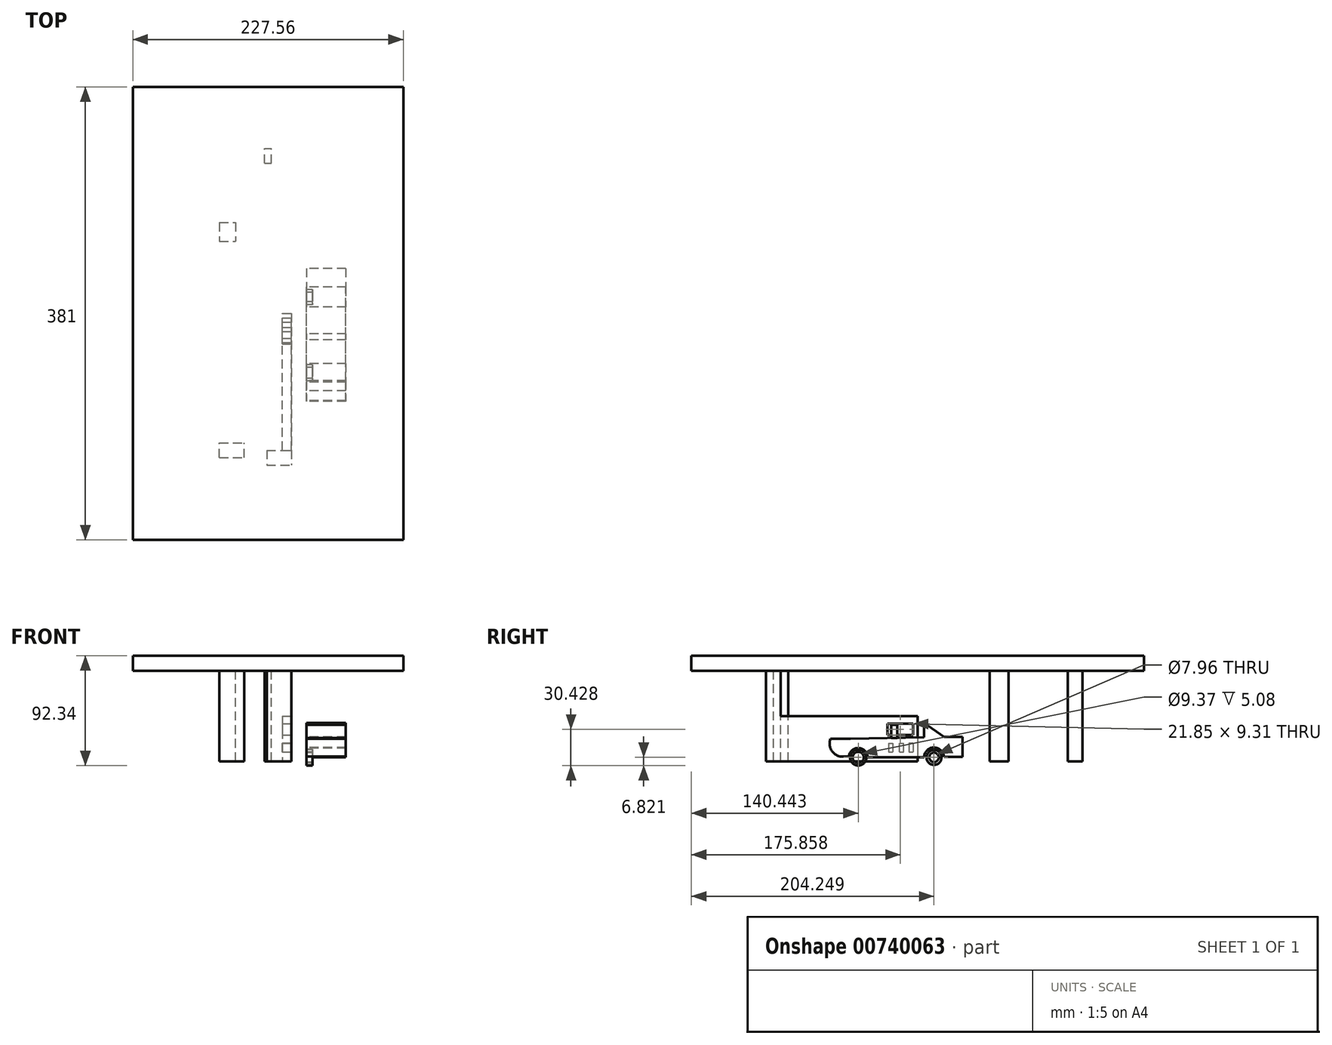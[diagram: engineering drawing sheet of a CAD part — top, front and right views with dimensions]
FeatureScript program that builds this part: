
annotation { "Feature Type Name" : "Feature", "Feature Type Description" : "" }
export const myFeature = defineFeature(function(context is Context, id is Id, definition is map)
    precondition{}
    {
        {
            var Q0;
            Q0=qCreatedBy(makeId("Top.planeOp"),FACE);
            var sketch = newSketch(context, id + "F0", { "sketchPlane" : qUnion([Q0])});
            skLineSegment(sketch, "E0.bottom", {"start": v(113.78, 190.5) * mm, "end": v(-113.78, 190.5) * mm});
            skLineSegment(sketch, "E0.top", {"start": v(113.78, -190.5) * mm, "end": v(-113.78, -190.5) * mm});
            skLineSegment(sketch, "E0.left", {"start": v(113.78, 190.5) * mm, "end": v(113.78, -190.5) * mm});
            skLineSegment(sketch, "E0.right", {"start": v(-113.78, 190.5) * mm, "end": v(-113.78, -190.5) * mm});
            skPoint(sketch, "E0.middle", {"position": v(0, 0) * mm});
            skSolve(sketch);
        }
        {
            var Q0;
            Q0=makeQuery(id+"F0.imprint","IMPRINT",FACE,{"disambiguationData":[TD([[makeQuery(id+"F0.imprint","IMPRINT",EDGE,{"derivedFrom":sQuery(id+"F0.wireOp",EDGE,"E0.bottom")}),1.0]])]});
            extrude(context, id + "F1", {"entities" : qUnion([Q0]), "depth" : 12.7 * mm, "offsetDistance" : 25.4 * mm});
        }
        {
            var Q0;
            Q0=makeQuery(id+"F1.opExtrude","CAP_FACE",FACE,{"disambiguationData":[OSD([sQuery(id+"F0.wireOp",EDGE,"E0.bottom"),sQuery(id+"F0.wireOp",EDGE,"E0.top"),sQuery(id+"F0.wireOp",EDGE,"E0.left"),sQuery(id+"F0.wireOp",EDGE,"E0.right")])],"isStart":true});
            var sketch = newSketch(context, id + "F2", { "sketchPlane" : qUnion([Q0])});
            skLineSegment(sketch, "E1.bottom", {"start": v(-2.86, -126.27) * mm, "end": v(2.86, -126.27) * mm});
            skLineSegment(sketch, "E1.top", {"start": v(-2.86, -138.66) * mm, "end": v(2.86, -138.66) * mm});
            skLineSegment(sketch, "E1.left", {"start": v(-2.86, -126.27) * mm, "end": v(-2.86, -138.66) * mm});
            skLineSegment(sketch, "E1.right", {"start": v(2.86, -126.27) * mm, "end": v(2.86, -138.66) * mm});
            skPoint(sketch, "E1.middle", {"position": v(0, -132.46) * mm});
            skLineSegment(sketch, "E2.bottom", {"start": v(-41.04, -76.38) * mm, "end": v(-27.55, -76.38) * mm});
            skLineSegment(sketch, "E2.top", {"start": v(-41.04, -60.63) * mm, "end": v(-27.55, -60.63) * mm});
            skLineSegment(sketch, "E2.left", {"start": v(-41.04, -76.38) * mm, "end": v(-41.04, -60.63) * mm});
            skLineSegment(sketch, "E2.right", {"start": v(-27.55, -76.38) * mm, "end": v(-27.55, -60.63) * mm});
            skPoint(sketch, "E2.middle", {"position": v(-34.3, -68.5) * mm});
            skLineSegment(sketch, "E3.bottom", {"start": v(-1.12, 115.21) * mm, "end": v(19.65, 115.21) * mm});
            skLineSegment(sketch, "E3.top", {"start": v(-1.12, 127.6) * mm, "end": v(19.65, 127.6) * mm});
            skLineSegment(sketch, "E3.left", {"start": v(-1.12, 115.21) * mm, "end": v(-1.12, 127.6) * mm});
            skLineSegment(sketch, "E3.right", {"start": v(19.65, 115.21) * mm, "end": v(19.65, 127.6) * mm});
            skPoint(sketch, "E3.middle", {"position": v(9.26, 121.4) * mm});
            skLineSegment(sketch, "E4.bottom", {"start": v(-41.04, 121.4) * mm, "end": v(-20.26, 121.4) * mm});
            skLineSegment(sketch, "E4.top", {"start": v(-41.04, 109.02) * mm, "end": v(-20.26, 109.02) * mm});
            skLineSegment(sketch, "E4.left", {"start": v(-41.04, 121.4) * mm, "end": v(-41.04, 109.02) * mm});
            skLineSegment(sketch, "E4.right", {"start": v(-20.26, 121.4) * mm, "end": v(-20.26, 109.02) * mm});
            skPoint(sketch, "E4.middle", {"position": v(-30.65, 115.21) * mm});
            skSolve(sketch);
        }
        {
            var Q0;
            Q0=makeQuery(id+"F2.imprint","IMPRINT",FACE,{"disambiguationData":[TD([[makeQuery(id+"F2.imprint","IMPRINT",EDGE,{"derivedFrom":sQuery(id+"F2.wireOp",EDGE,"E1.bottom")}),-1.0]])]});
            var Q1;
            Q1=makeQuery(id+"F2.imprint","IMPRINT",FACE,{"disambiguationData":[TD([[makeQuery(id+"F2.imprint","IMPRINT",EDGE,{"derivedFrom":sQuery(id+"F2.wireOp",EDGE,"E2.bottom")}),1.0]])]});
            extrude(context, id + "F3", {"entities" : qUnion([Q0, Q1]), "operationType" : NewBodyOperationType.ADD, "depth" : 25.4 * mm, "offsetDistance" : 25.4 * mm});
        }
        {
            var Q0;
            Q0 = qSketchRegion(id + "F2", true);
            extrude(context, id + "F4", {"entities" : qUnion([Q0]), "operationType" : NewBodyOperationType.ADD, "depth" : 76.2 * mm, "offsetDistance" : 25.4 * mm});
        }
        {
            var Q0;
            Q0=makeQuery(id+"F4.opExtrude","SWEPT_FACE",FACE,{"disambiguationData":[OSD([sQuery(id+"F2.wireOp",EDGE,"E3.right")])]});
            var sketch = newSketch(context, id + "F5", { "sketchPlane" : qUnion([Q0])});
            skLineSegment(sketch, "E5.bottom", {"start": v(-115.21, -38.1) * mm, "end": v(0, -38.1) * mm});
            skLineSegment(sketch, "E5.top", {"start": v(-115.21, -76.2) * mm, "end": v(0, -76.2) * mm});
            skLineSegment(sketch, "E5.left", {"start": v(-115.21, -38.1) * mm, "end": v(-115.21, -76.2) * mm});
            skLineSegment(sketch, "E5.right", {"start": v(0, -38.1) * mm, "end": v(0, -76.2) * mm});
            skSolve(sketch);
        }
        {
            var Q0;
            Q0=makeQuery(id+"F5.imprint","IMPRINT",FACE,{"disambiguationData":[TD([[makeQuery(id+"F5.imprint","IMPRINT",EDGE,{"derivedFrom":sQuery(id+"F5.wireOp",EDGE,"E5.bottom")}),-1.0]])]});
            extrude(context, id + "F6", {"entities" : qUnion([Q0]), "operationType" : NewBodyOperationType.ADD, "oppositeDirection" : true, "depth" : 7.62 * mm, "offsetDistance" : 25.4 * mm});
        }
        {
            var Q0;
            Q0=makeQuery(id+"F6.boolean.opBoolean","MERGE",FACE,{"derivedFrom":[makeQuery(id+"F4.opExtrude","SWEPT_FACE",FACE,{"disambiguationData":[OSD([sQuery(id+"F2.wireOp",EDGE,"E3.right")])]}),makeQuery(id+"F6.opExtrude","CAP_FACE",FACE,{"disambiguationData":[OSD([sQuery(id+"F5.wireOp",EDGE,"E5.bottom"),sQuery(id+"F5.wireOp",EDGE,"E5.top"),sQuery(id+"F5.wireOp",EDGE,"E5.left"),sQuery(id+"F5.wireOp",EDGE,"E5.right")])],"isStart":true})]});
            var sketch = newSketch(context, id + "F7", { "sketchPlane" : qUnion([Q0])});
            skLineSegment(sketch, "E6.bottom", {"start": v(-25.57, -44.56) * mm, "end": v(-3.72, -44.56) * mm});
            skLineSegment(sketch, "E6.top", {"start": v(-25.57, -53.87) * mm, "end": v(-3.72, -53.87) * mm});
            skLineSegment(sketch, "E6.left", {"start": v(-25.57, -44.56) * mm, "end": v(-25.57, -53.87) * mm});
            skLineSegment(sketch, "E6.right", {"start": v(-3.72, -44.56) * mm, "end": v(-3.72, -53.87) * mm});
            skLineSegment(sketch, "E7.bottom", {"start": v(-24.37, -61.07) * mm, "end": v(-21.08, -61.07) * mm});
            skLineSegment(sketch, "E7.top", {"start": v(-24.37, -68.26) * mm, "end": v(-21.08, -68.26) * mm});
            skLineSegment(sketch, "E7.left", {"start": v(-24.37, -61.07) * mm, "end": v(-24.37, -68.26) * mm});
            skLineSegment(sketch, "E7.right", {"start": v(-21.08, -61.07) * mm, "end": v(-21.08, -68.26) * mm});
            skLineSegment(sketch, "E8.bottom", {"start": v(-15.4, -68.26) * mm, "end": v(-11.8, -68.26) * mm});
            skLineSegment(sketch, "E8.top", {"start": v(-15.4, -60.85) * mm, "end": v(-11.8, -60.85) * mm});
            skLineSegment(sketch, "E8.left", {"start": v(-15.4, -68.26) * mm, "end": v(-15.4, -60.85) * mm});
            skLineSegment(sketch, "E8.right", {"start": v(-11.8, -68.26) * mm, "end": v(-11.8, -60.85) * mm});
            skLineSegment(sketch, "E9.bottom", {"start": v(-7.3, -60.64) * mm, "end": v(-3.72, -60.64) * mm});
            skLineSegment(sketch, "E9.top", {"start": v(-7.3, -68.26) * mm, "end": v(-3.72, -68.26) * mm});
            skLineSegment(sketch, "E9.left", {"start": v(-7.3, -60.64) * mm, "end": v(-7.3, -68.26) * mm});
            skLineSegment(sketch, "E9.right", {"start": v(-3.72, -60.64) * mm, "end": v(-3.72, -68.26) * mm});
            skSolve(sketch);
        }
        {
            var Q0;
            Q0=makeQuery(id+"F7.imprint","IMPRINT",FACE,{"disambiguationData":[TD([[makeQuery(id+"F7.imprint","IMPRINT",EDGE,{"derivedFrom":sQuery(id+"F7.wireOp",EDGE,"E6.bottom")}),-1.0]])]});
            var Q1;
            Q1=makeQuery(id+"F7.imprint","IMPRINT",FACE,{"disambiguationData":[TD([[makeQuery(id+"F7.imprint","IMPRINT",EDGE,{"derivedFrom":sQuery(id+"F7.wireOp",EDGE,"E7.bottom")}),-1.0]])]});
            var Q2;
            Q2=makeQuery(id+"F7.imprint","IMPRINT",FACE,{"disambiguationData":[TD([[makeQuery(id+"F7.imprint","IMPRINT",EDGE,{"derivedFrom":sQuery(id+"F7.wireOp",EDGE,"E8.bottom")}),1.0]])]});
            var Q3;
            Q3=makeQuery(id+"F7.imprint","IMPRINT",FACE,{"disambiguationData":[TD([[makeQuery(id+"F7.imprint","IMPRINT",EDGE,{"derivedFrom":sQuery(id+"F7.wireOp",EDGE,"E9.bottom")}),-1.0]])]});
            extrude(context, id + "F8", {"entities" : qUnion([Q0, Q1, Q2, Q3]), "operationType" : NewBodyOperationType.REMOVE, "endBound" : BoundingType.THROUGH_ALL, "oppositeDirection" : true, "depth" : 25.4 * mm, "offsetDistance" : 25.4 * mm});
        }
        {
            var Q0;
            Q0=makeQuery(id+"F6.boolean.opBoolean","MERGE",FACE,{"derivedFrom":[makeQuery(id+"F4.opExtrude","CAP_FACE",FACE,{"disambiguationData":[OSD([sQuery(id+"F2.wireOp",EDGE,"E3.bottom"),sQuery(id+"F2.wireOp",EDGE,"E3.top"),sQuery(id+"F2.wireOp",EDGE,"E3.left"),sQuery(id+"F2.wireOp",EDGE,"E3.right")])],"isStart":false}),makeQuery(id+"F6.opExtrude","SWEPT_FACE",FACE,{"disambiguationData":[OSD([sQuery(id+"F5.wireOp",EDGE,"E5.top")])]})]});
            cPlane(context, id + "F9", {"entities" : qUnion([Q0]), "cplaneType" : CPlaneType.OFFSET, "offset" : 0 * mm, "width" : 152.4 * mm, "height" : 152.4 * mm});
        }
        {
            var Q0;
            Q0=makeQuery(id+"F6.boolean.opBoolean","MERGE",FACE,{"derivedFrom":[makeQuery(id+"F4.opExtrude","SWEPT_FACE",FACE,{"disambiguationData":[OSD([sQuery(id+"F2.wireOp",EDGE,"E3.right")])]}),makeQuery(id+"F6.opExtrude","CAP_FACE",FACE,{"disambiguationData":[OSD([sQuery(id+"F5.wireOp",EDGE,"E5.bottom"),sQuery(id+"F5.wireOp",EDGE,"E5.top"),sQuery(id+"F5.wireOp",EDGE,"E5.left"),sQuery(id+"F5.wireOp",EDGE,"E5.right")])],"isStart":true})]});
            cPlane(context, id + "F10", {"entities" : qUnion([Q0]), "cplaneType" : CPlaneType.OFFSET, "offset" : 12.7 * mm, "width" : 152.4 * mm, "height" : 152.4 * mm});
        }
        {
            var Q0;
            Q0=qCreatedBy(id+"F10.planeOp",FACE);
            var sketch = newSketch(context, id + "F11", { "sketchPlane" : qUnion([Q0])});
            skLineSegment(sketch, "E10.bottom", {"start": v(-42.15, -72.82) * mm, "end": v(5.4, -72.82) * mm});
            skLineSegment(sketch, "E10.right", {"start": v(5.4, -72.82) * mm, "end": v(5.4, -43.7) * mm});
            skLineSegment(sketch, "E11", {"start": v(-56.6, -57.26) * mm, "end": v(-73.5, -57.26) * mm});
            skArc(sketch, "E12", {"start": v(-73.5, -57.26) * mm, "mid": v(-72.62, -66.61) * mm, "end": v(-65.04, -72.15) * mm});
            skPoint(sketch, "E12.endSnap0", {"position": v(-65.04, -57.26) * mm});
            skLineSegment(sketch, "E13", {"start": v(-65.04, -72.15) * mm, "end": v(-57.93, -72.15) * mm});
            skArc(sketch, "E14", {"start": v(-42.15, -72.82) * mm, "mid": v(-49.72, -64.92) * mm, "end": v(-57.93, -72.15) * mm});
            skLineSegment(sketch, "E15", {"start": v(5.4, -43.7) * mm, "end": v(22.08, -55.48) * mm});
            skLineSegment(sketch, "E16", {"start": v(22.08, -55.48) * mm, "end": v(37.86, -55.48) * mm});
            skLineSegment(sketch, "E17", {"start": v(37.86, -55.48) * mm, "end": v(37.86, -72.37) * mm});
            skLineSegment(sketch, "E18", {"start": v(37.86, -72.37) * mm, "end": v(22.08, -72.37) * mm});
            skArc(sketch, "E19", {"start": v(22.08, -72.37) * mm, "mid": v(13.53, -64.48) * mm, "end": v(5.4, -72.82) * mm});
            skCircle(sketch, "E20", {"center": v(-50.06, -72.82) * mm, "radius": 6.82 * mm});
            skCircle(sketch, "E21", {"center": v(-50.06, -72.82) * mm, "radius": 4.69 * mm});
            skCircle(sketch, "E22", {"center": v(13.75, -72.82) * mm, "radius": 6.33 * mm});
            skCircle(sketch, "E23", {"center": v(13.75, -72.82) * mm, "radius": 3.98 * mm});
            skLineSegment(sketch, "E24", {"start": v(-50.06, -72.82) * mm, "end": v(-50.06, -68.13) * mm});
            skLineSegment(sketch, "E25", {"start": v(-50.06, -72.82) * mm, "end": v(-54.74, -72.82) * mm});
            skLineSegment(sketch, "E26", {"start": v(-50.06, -72.82) * mm, "end": v(-50.06, -77.5) * mm});
            skLineSegment(sketch, "E27", {"start": v(-50.06, -72.82) * mm, "end": v(-45.37, -72.82) * mm});
            skLineSegment(sketch, "E28", {"start": v(13.75, -72.82) * mm, "end": v(13.75, -68.84) * mm});
            skLineSegment(sketch, "E29", {"start": v(-50.06, -72.82) * mm, "end": v(-46.66, -69.6) * mm});
            skLineSegment(sketch, "E30", {"start": v(-50.06, -72.82) * mm, "end": v(-53.28, -69.42) * mm});
            skLineSegment(sketch, "E31", {"start": v(13.75, -72.82) * mm, "end": v(13.75, -76.8) * mm});
            skLineSegment(sketch, "E32", {"start": v(13.75, -72.82) * mm, "end": v(17.73, -72.82) * mm});
            skLineSegment(sketch, "E33", {"start": v(13.75, -72.82) * mm, "end": v(9.77, -72.82) * mm});
            skLineSegment(sketch, "E34", {"start": v(-50.06, -72.82) * mm, "end": v(-53.46, -76.04) * mm});
            skLineSegment(sketch, "E35", {"start": v(-50.06, -72.82) * mm, "end": v(-46.83, -76.22) * mm});
            skLineSegment(sketch, "E36", {"start": v(-56.6, -57.26) * mm, "end": v(22.08, -55.48) * mm});
            skPoint(sketch, "E37.startSnap0", {"position": v(-17.26, -56.37) * mm});
            skLineSegment(sketch, "E38.bottom", {"start": v(-17.26, -56.37) * mm, "end": v(-22.37, -56.37) * mm});
            skLineSegment(sketch, "E38.top", {"start": v(-17.26, -45.26) * mm, "end": v(-22.37, -45.26) * mm});
            skLineSegment(sketch, "E38.left", {"start": v(-17.26, -56.37) * mm, "end": v(-17.26, -45.26) * mm});
            skLineSegment(sketch, "E38.right", {"start": v(-22.37, -56.37) * mm, "end": v(-22.37, -45.26) * mm});
            skSolve(sketch);
        }
        {
            var Q0;
            {var subQ2=sQuery(id+"F11.wireOp",EDGE,"E10.bottom");Q0=makeQuery(id+"F11.imprint","IMPRINT",FACE,{"disambiguationData":[TD([[makeQuery(id+"F11.imprint","IMPRINT",EDGE,{"derivedFrom":subQ2}),1.0]])]});}
            var Q1;
            {var subQ0=sQuery(id+"F11.wireOp",EDGE,"E16");Q1=makeQuery(id+"F11.imprint","IMPRINT",FACE,{"disambiguationData":[TD([[makeQuery(id+"F11.imprint","IMPRINT",EDGE,{"derivedFrom":subQ0}),-1.0]])]});}
            var Q2;
            Q2=makeQuery(id+"F11.imprint","IMPRINT",FACE,{"disambiguationData":[TD([[makeQuery(id+"F11.imprint","IMPRINT",EDGE,{"derivedFrom":sQuery(id+"F11.wireOp",EDGE,"E38.bottom")}),-1.0]])]});
            extrude(context, id + "F12", {"entities" : qUnion([Q0, Q1, Q2]), "depth" : 33.02 * mm, "offsetDistance" : 25.4 * mm});
        }
        {
            var Q0;
            Q0=makeQuery(id+"F11.imprint","IMPRINT",FACE,{"disambiguationData":[TD([[makeQuery(id+"F11.imprint","IMPRINT",EDGE,{"derivedFrom":sQuery(id+"F11.wireOp",EDGE,"E20")}),1.0]])]});
            var Q1;
            Q1=makeQuery(id+"F11.imprint","IMPRINT",FACE,{"disambiguationData":[TD([[makeQuery(id+"F11.imprint","IMPRINT",EDGE,{"derivedFrom":sQuery(id+"F11.wireOp",EDGE,"E22")}),1.0]])]});
            extrude(context, id + "F13", {"entities" : qUnion([Q0, Q1]), "depth" : 5.08 * mm, "offsetDistance" : 25.4 * mm});
        }
        {
            var Q0;
            {var subQ0=sQuery(id+"F11.wireOp",EDGE,"E15");Q0=makeQuery(id+"F11.imprint","IMPRINT",FACE,{"disambiguationData":[TD([[makeQuery(id+"F11.imprint","IMPRINT",EDGE,{"derivedFrom":subQ0}),-1.0]])]});}
            extrude(context, id + "F14", {"entities" : qUnion([Q0]), "operationType" : NewBodyOperationType.ADD, "depth" : 33.02 * mm, "offsetDistance" : 25.4 * mm});
        }
    });
